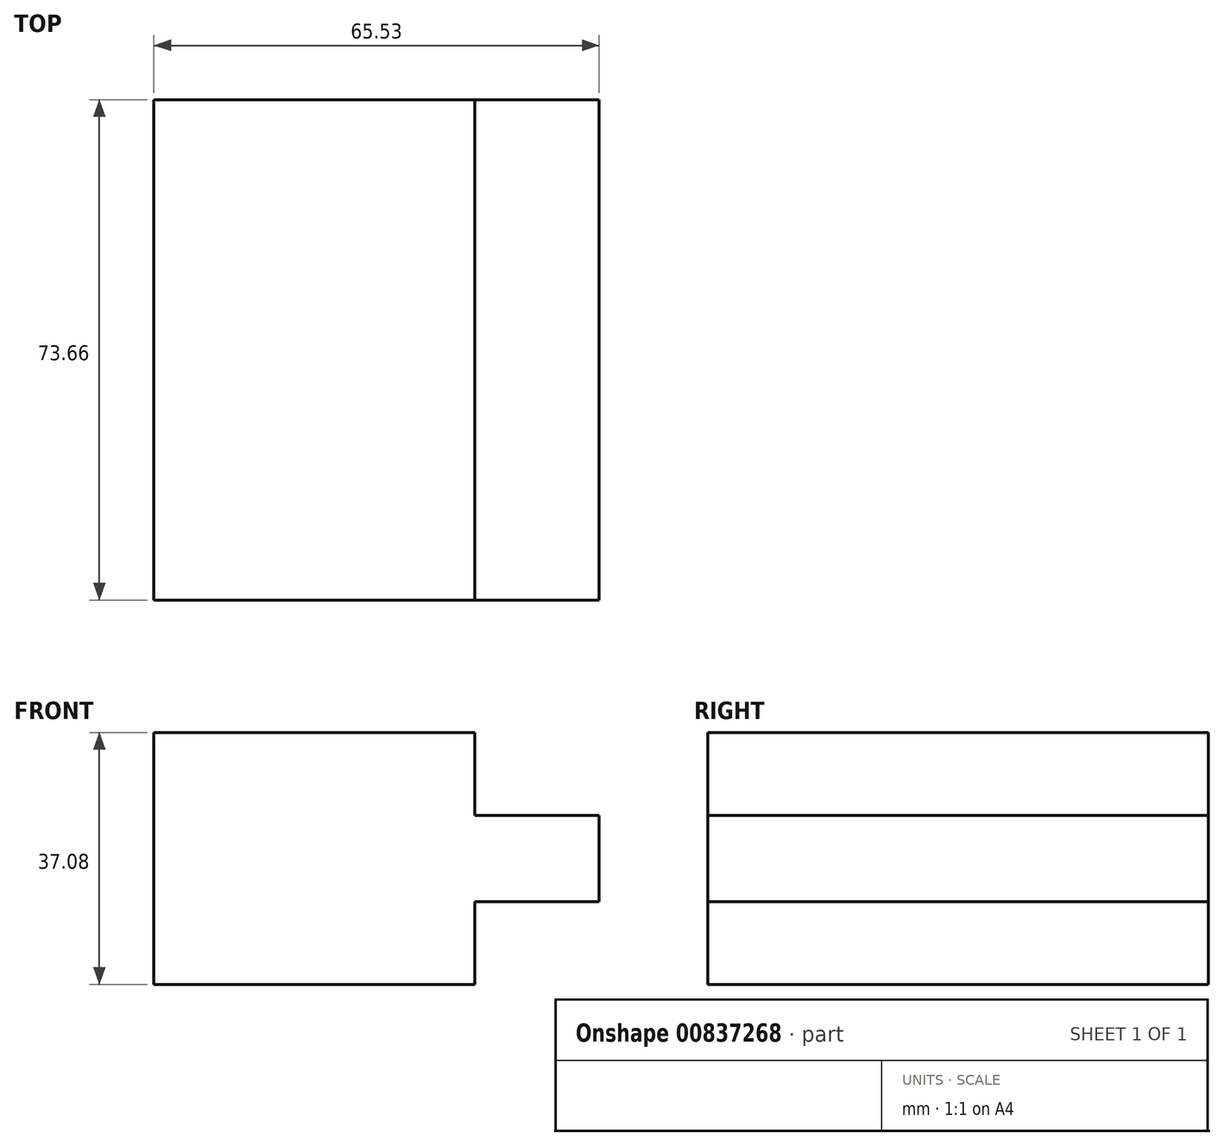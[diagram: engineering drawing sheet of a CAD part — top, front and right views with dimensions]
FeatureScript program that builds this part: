
annotation { "Feature Type Name" : "Feature", "Feature Type Description" : "" }
export const myFeature = defineFeature(function(context is Context, id is Id, definition is map)
    precondition{}
    {
        {
            var Q0;
            Q0=qCreatedBy(makeId("Top.planeOp"),FACE);
            var sketch = newSketch(context, id + "F0", { "sketchPlane" : qUnion([Q0])});
            skLineSegment(sketch, "E0.bottom", {"start": v(-85.34, 37.86) * mm, "end": v(-38.1, 37.86) * mm});
            skLineSegment(sketch, "E0.top", {"start": v(-85.34, -35.8) * mm, "end": v(-38.1, -35.8) * mm});
            skLineSegment(sketch, "E0.left", {"start": v(-85.34, 37.86) * mm, "end": v(-85.34, -35.8) * mm});
            skLineSegment(sketch, "E0.right", {"start": v(-38.1, 37.86) * mm, "end": v(-38.1, -35.8) * mm});
            skSolve(sketch);
        }
        {
            var Q0;
            Q0=makeQuery(id+"F0.imprint","IMPRINT",FACE,{"disambiguationData":[TD([[makeQuery(id+"F0.imprint","IMPRINT",EDGE,{"derivedFrom":sQuery(id+"F0.wireOp",EDGE,"E0.bottom")}),-1.0]])]});
            extrude(context, id + "F1", {"entities" : qUnion([Q0]), "depth" : 37.08 * mm, "offsetDistance" : 25.4 * mm});
        }
        {
            var Q0;
            Q0=makeQuery(id+"F1.opExtrude","SWEPT_FACE",FACE,{"disambiguationData":[OSD([sQuery(id+"F0.wireOp",EDGE,"E0.right")])]});
            var sketch = newSketch(context, id + "F2", { "sketchPlane" : qUnion([Q0])});
            skLineSegment(sketch, "E1", {"start": v(-35.8, 18.54) * mm, "end": v(37.86, 18.54) * mm, "construction": true});
            skLineSegment(sketch, "E2.bottom", {"start": v(-35.8, 24.9) * mm, "end": v(37.86, 24.9) * mm});
            skLineSegment(sketch, "E2.top", {"start": v(-35.8, 12.2) * mm, "end": v(37.86, 12.2) * mm});
            skLineSegment(sketch, "E2.left", {"start": v(-35.8, 24.9) * mm, "end": v(-35.8, 12.2) * mm});
            skLineSegment(sketch, "E2.right", {"start": v(37.86, 24.9) * mm, "end": v(37.86, 12.2) * mm});
            skSolve(sketch);
        }
        {
            var Q0;
            Q0=makeQuery(id+"F2.imprint","IMPRINT",FACE,{"disambiguationData":[TD([[makeQuery(id+"F2.imprint","IMPRINT",EDGE,{"derivedFrom":sQuery(id+"F2.wireOp",EDGE,"E2.bottom")}),-1.0]])]});
            extrude(context, id + "F3", {"entities" : qUnion([Q0]), "operationType" : NewBodyOperationType.ADD, "depth" : 18.29 * mm, "offsetDistance" : 25.4 * mm});
        }
    });
